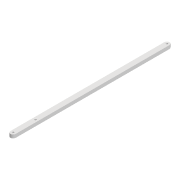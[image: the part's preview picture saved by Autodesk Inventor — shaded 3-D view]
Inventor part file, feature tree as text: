
AUTODESK INVENTOR PART (.ipt)
format: ipt  version: 2022 (Build 260153000, 153)  size: 93,184 bytes
history: native  units: mm
features: extrude x1, sketch x1
ambient origin geometry x8: Origin, YZ Plane, XZ Plane, XY Plane, X Axis, Y Axis, Z Axis, Center Point
bodies: Solid1 (feature_tree)
feature tree (2):
  extrude  "Extrusion1"  Depth=26.043mm
  sketch  "Sketch1"  dims[d0=2.2mm d1=2.2mm d2=6.0mm d3=180.271mm d6=4.0mm d7=0.0mm d14=2.2mm d15=26.043mm]
